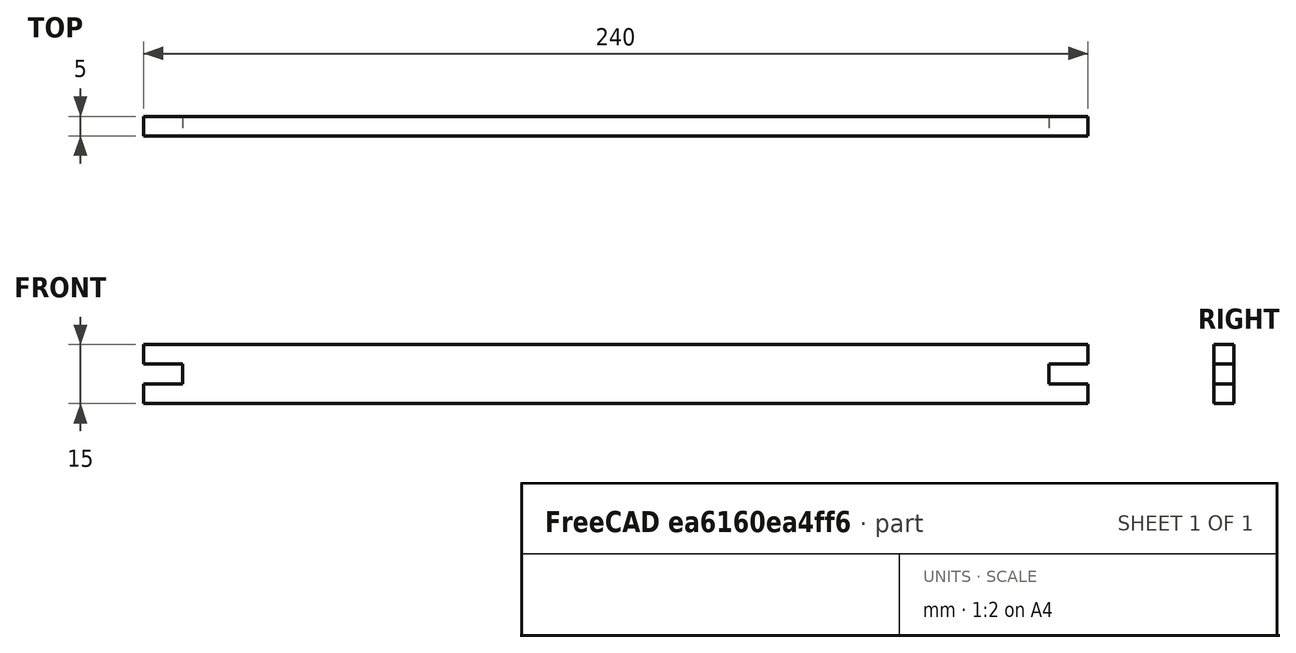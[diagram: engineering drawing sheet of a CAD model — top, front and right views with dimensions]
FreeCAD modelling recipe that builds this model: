
FCSTD DOCUMENT  (FreeCAD 1.0R39319 (Git))
Label: X Axis Far Leg
License: All rights reserved
LicenseURL: https://en.wikipedia.org/wiki/All_rights_reserved
objects: PartDesign::CoordinateSystem×2, Sketcher::SketchObject×1, PartDesign::Pad×1, PartDesign::Body×1, App::Part×1
note: 8 computed .brp shape members not serialized (recipe doc carries the construction recipe); baked Part::Feature solids carry a one-line shape summary decoded from their .brp

FEATURE [Sketcher::SketchObject] Sketch
  ArcFitTolerance = 1e-06
  AttachmentSupport = -> [XZ_Plane001]
  FullyConstrained = true
  MakeInternals = false
  MapMode = 5
  Placement = pos=(0,0,0) rot=(1,0,0;1.5708rad)
  sketch-geometry (14):
    g0: LineSegment StartX=0 StartY=7.5 StartZ=0 EndX=0 EndY=2.55 EndZ=0
    g1: LineSegment StartX=0 StartY=-7.5 StartZ=0 EndX=240 EndY=-7.5 EndZ=0
    g2: LineSegment StartX=240 StartY=-7.5 StartZ=0 EndX=240 EndY=-2.55 EndZ=0
    g3: LineSegment StartX=240 StartY=7.5 StartZ=0 EndX=0 EndY=7.5 EndZ=0
    g4: LineSegment StartX=0 StartY=2.55 StartZ=0 EndX=10 EndY=2.55 EndZ=0
    g5: LineSegment StartX=10 StartY=2.55 StartZ=0 EndX=10 EndY=-2.55 EndZ=0
    g6: LineSegment StartX=10 StartY=-2.55 StartZ=0 EndX=0 EndY=-2.55 EndZ=0
    g7: LineSegment StartX=0 StartY=-2.55 StartZ=0 EndX=0 EndY=-7.5 EndZ=0
    g8: GeomPoint [constr] X=10 Y=0 Z=0
    g9: LineSegment StartX=240 StartY=2.55 StartZ=0 EndX=230 EndY=2.55 EndZ=0
    g10: LineSegment StartX=230 StartY=2.55 StartZ=0 EndX=230 EndY=-2.55 EndZ=0
    g11: LineSegment StartX=230 StartY=-2.55 StartZ=0 EndX=240 EndY=-2.55 EndZ=0
    g12: LineSegment StartX=240 StartY=2.55 StartZ=0 EndX=240 EndY=7.5 EndZ=0
    g13: GeomPoint [constr] X=230 Y=4e-16 Z=0
  constraints (40):
    c: Coincident(g7,g1)
    c: Coincident(g1,g2)
    c: Coincident(g12,g3)
    c: Coincident(g3,g0)
    c: Vertical(g0)
    c: Vertical(g2)
    c: Horizontal(g1)
    c: Horizontal(g3)
    c: DistanceX(g3,g3) = 240
    c: Distance(g2,g12) = 15
    c: Horizontal(g4)
    c: Coincident(g4,g5)
    c: Vertical(g5)
    c: Coincident(g5,g6)
    c: PointOnObject(g6,g7)
    c: Horizontal(g6)
    c: Coincident(g0,g4)
    c: PointOnObject(g7,g6)
    c: DistanceX(g4,g4) = 10
    c: Symmetric(g5,g5,g8)
    c: Distance(g8,g3) = 7.5
    c: Distance(g6,g4) = 5.1
    c: PointOnObject(g0,g7)
    c: Vertical(g7)
    c: PointOnObject(g9,g12)
    c: Horizontal(g9)
    c: Coincident(g9,g10)
    c: Vertical(g10)
    c: Coincident(g10,g11)
    c: Horizontal(g11)
    c: Coincident(g2,g11)
    c: PointOnObject(g12,g9)
    c: DistanceX(g9,g9) = 10
    c: Vertical(g12)
    c: Distance(g11,g9) = 5.1
    c: PointOnObject(g9,g2)
    c: Symmetric(g10,g10,g13)
    c: Distance(g13,g3) = 7.5
    c: PointOnObject(g8,g-1)
    c: PointOnObject(g0,g-2)
FEATURE [PartDesign::Pad] Pad
  Direction = (0,-1,2e-16)
  Length = 5
  Length2 = 10
  Midplane = true
  Placement = pos=(0,0,0) rot=(1,0,0;1.5708rad)
  Profile = -> Sketch
  ReferenceAxis = -> Sketch [N_Axis]
  Refine = true
  Suppressed = false
  Type = 0
FEATURE [PartDesign::Body] Body  label="X Axis Far Leg001"
  AllowCompound = false
  Group = -> [Sketch,Pad]
  Origin = -> Origin001
  Tip = -> Pad
FEATURE [PartDesign::CoordinateSystem] LCS_1
  AttacherType = Attacher::AttachEngine3D
  AttachmentOffset = pos=(10,0,0) rot=(0,0,1;0rad)
  AttachmentSupport = -> [XY_Plane001]
  MapMode = 2
  Placement = pos=(10,0,0) rot=(0,0,1;0rad)
FEATURE [PartDesign::CoordinateSystem] LCS_2
  AttacherType = Attacher::AttachEngine3D
  AttachmentOffset = pos=(230,0,0) rot=(0,0,1;0rad)
  AttachmentSupport = -> [XY_Plane001]
  MapMode = 2
  Placement = pos=(230,0,0) rot=(0,0,1;0rad)
FEATURE [App::Part] Part  label="X Axis Far Leg"
  Group = -> [Body,LCS_1,LCS_2]
  Origin = -> Origin
